# Revit family: revitupgrade
name_source: partatom
category: Furniture
units: mm (PartAtom-declared; Revit-internal decimal feet)

## family parameters
Always vertical = Yes
Cut with Voids When Loaded = No
Enable Cutting in Views = No
OmniClass Number = 23.40.70.14.64.11
OmniClass Title = Office Furniture
Render Appearance Source = Family Geometry
Room Calculation Point = No
Shared = No
Work Plane-Based = No

## types (1)
- H725 x W870 x D920mm
    Assembly Code = E2020200
    Default Elevation = 0.00 mm
    Depth = 920.00 mm
    Description = The Panorama modular sofa is designed to be an organic fit for any space, be it grand or large. Simply configure and combine its modules exactly as you’d like. While its curves allow for it to bring a modern touch to the scenery, its inherent comfort invites the user in for a seat that can be enhanced through loose cushions.
    Height = 725.00 mm
    Legs Finish = Wendelbo_Wood_BlackStainedOak
    Manufacturer = Wendelbo
    Release Date = September 2022
    Style Number(s) = WBOPANOSF1, WBOPANOSF2
    URL = https://www.steelcase.com
    Width = 870.00 mm

## geometry (parser evidence)
native form markers: Sweep x3
no freeform markers — native parametric forms only
